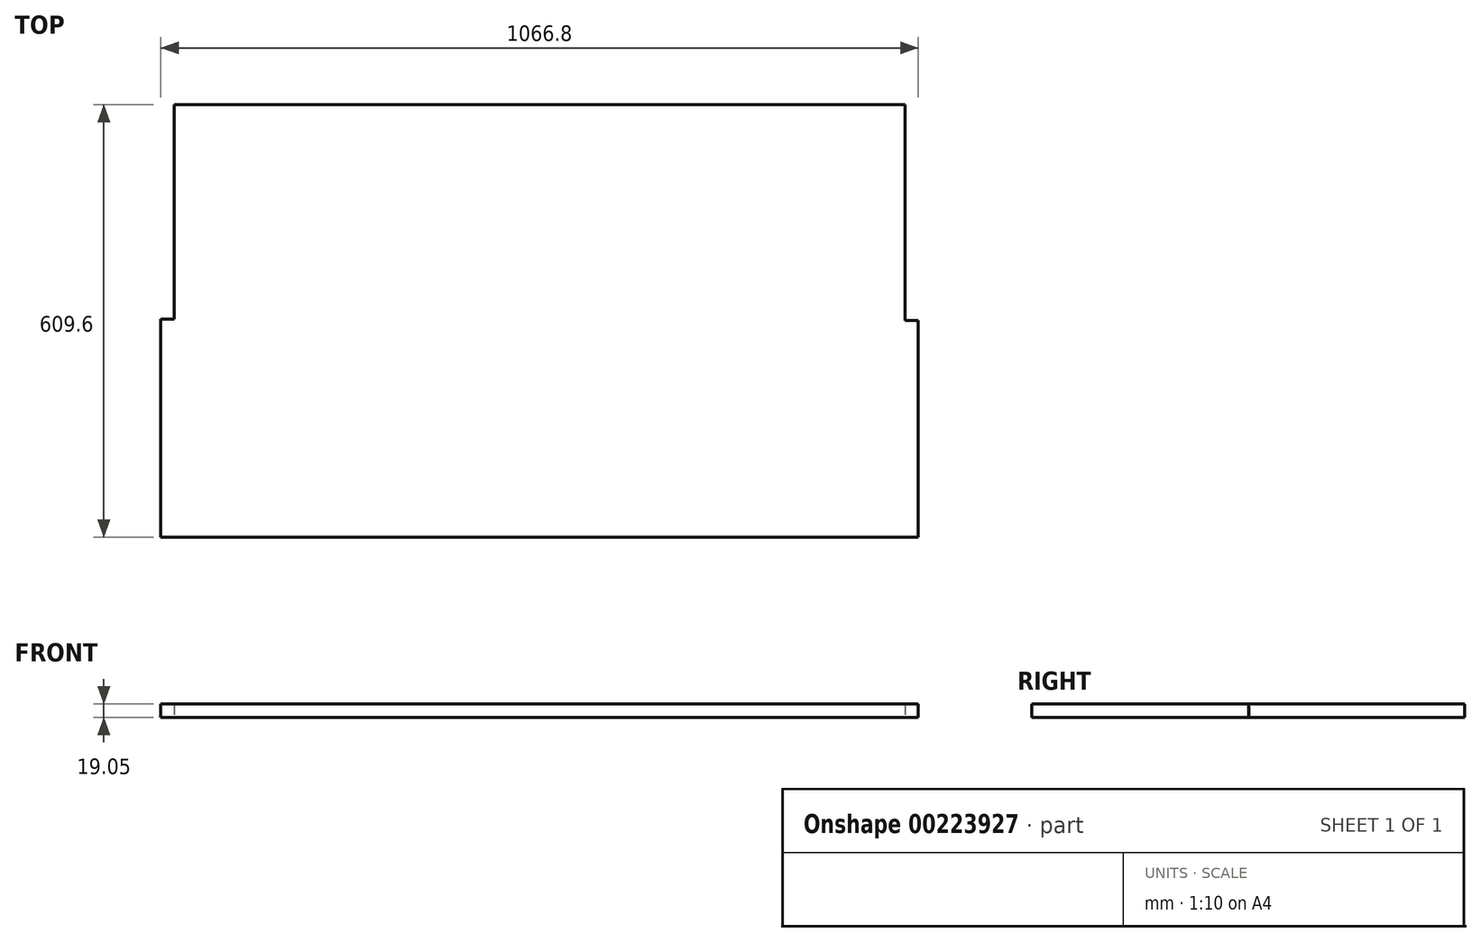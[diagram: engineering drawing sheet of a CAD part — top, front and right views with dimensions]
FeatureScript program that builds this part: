
annotation { "Feature Type Name" : "Feature", "Feature Type Description" : "" }
export const myFeature = defineFeature(function(context is Context, id is Id, definition is map)
    precondition{}
    {
        {
            var Q0;
            Q0=qCreatedBy(makeId("Top.planeOp"),FACE);
            var sketch = newSketch(context, id + "F0", { "sketchPlane" : qUnion([Q0])});
            skLineSegment(sketch, "E0.bottom", {"start": v(0, 0) * mm, "end": v(1066.8, 0) * mm});
            skLineSegment(sketch, "E0.top", {"start": v(0, 609.6) * mm, "end": v(1066.8, 609.6) * mm});
            skLineSegment(sketch, "E0.left", {"start": v(0, 0) * mm, "end": v(0, 609.6) * mm});
            skLineSegment(sketch, "E0.right", {"start": v(1066.8, 0) * mm, "end": v(1066.8, 609.6) * mm});
            skSolve(sketch);
        }
        {
            var Q0;
            Q0 = qSketchRegion(id + "F0", true);
            extrude(context, id + "F1", {"entities" : qUnion([Q0]), "oppositeDirection" : true, "depth" : 19.05 * mm});
        }
        {
            var Q0;
            Q0=qCreatedBy(makeId("Top.planeOp"),FACE);
            var sketch = newSketch(context, id + "F2", { "sketchPlane" : qUnion([Q0])});
            skLineSegment(sketch, "E1.bottom", {"start": v(0, 611.86) * mm, "end": v(19.05, 611.86) * mm});
            skLineSegment(sketch, "E1.top", {"start": v(0, 307.06) * mm, "end": v(19.05, 307.06) * mm});
            skLineSegment(sketch, "E1.left", {"start": v(0, 611.86) * mm, "end": v(0, 307.06) * mm});
            skLineSegment(sketch, "E1.right", {"start": v(19.05, 611.86) * mm, "end": v(19.05, 307.06) * mm});
            skPoint(sketch, "E2.firstSnap0", {"position": v(19.05, 459.46) * mm});
            skLineSegment(sketch, "E3.bottom", {"start": v(1067.5, 609.95) * mm, "end": v(1048.45, 609.95) * mm});
            skLineSegment(sketch, "E3.top", {"start": v(1067.5, 305.15) * mm, "end": v(1048.45, 305.15) * mm});
            skLineSegment(sketch, "E3.left", {"start": v(1067.5, 609.95) * mm, "end": v(1067.5, 305.15) * mm});
            skLineSegment(sketch, "E3.right", {"start": v(1048.45, 609.95) * mm, "end": v(1048.45, 305.15) * mm});
            skSolve(sketch);
        }
        {
            var Q0;
            Q0=makeQuery(id+"F2.imprint","IMPRINT",FACE,{"disambiguationData":[TD([[makeQuery(id+"F2.imprint","IMPRINT",EDGE,{"derivedFrom":sQuery(id+"F2.wireOp",EDGE,"E1.bottom")}),-1.0]])]});
            var Q1;
            Q1=makeQuery(id+"F2.imprint","IMPRINT",FACE,{"disambiguationData":[TD([[makeQuery(id+"F2.imprint","IMPRINT",EDGE,{"derivedFrom":sQuery(id+"F2.wireOp",EDGE,"E3.bottom")}),1.0]])]});
            extrude(context, id + "F3", {"entities" : qUnion([Q0, Q1]), "operationType" : NewBodyOperationType.REMOVE, "endBound" : BoundingType.THROUGH_ALL, "oppositeDirection" : true, "depth" : 25.4 * mm});
        }
    });
